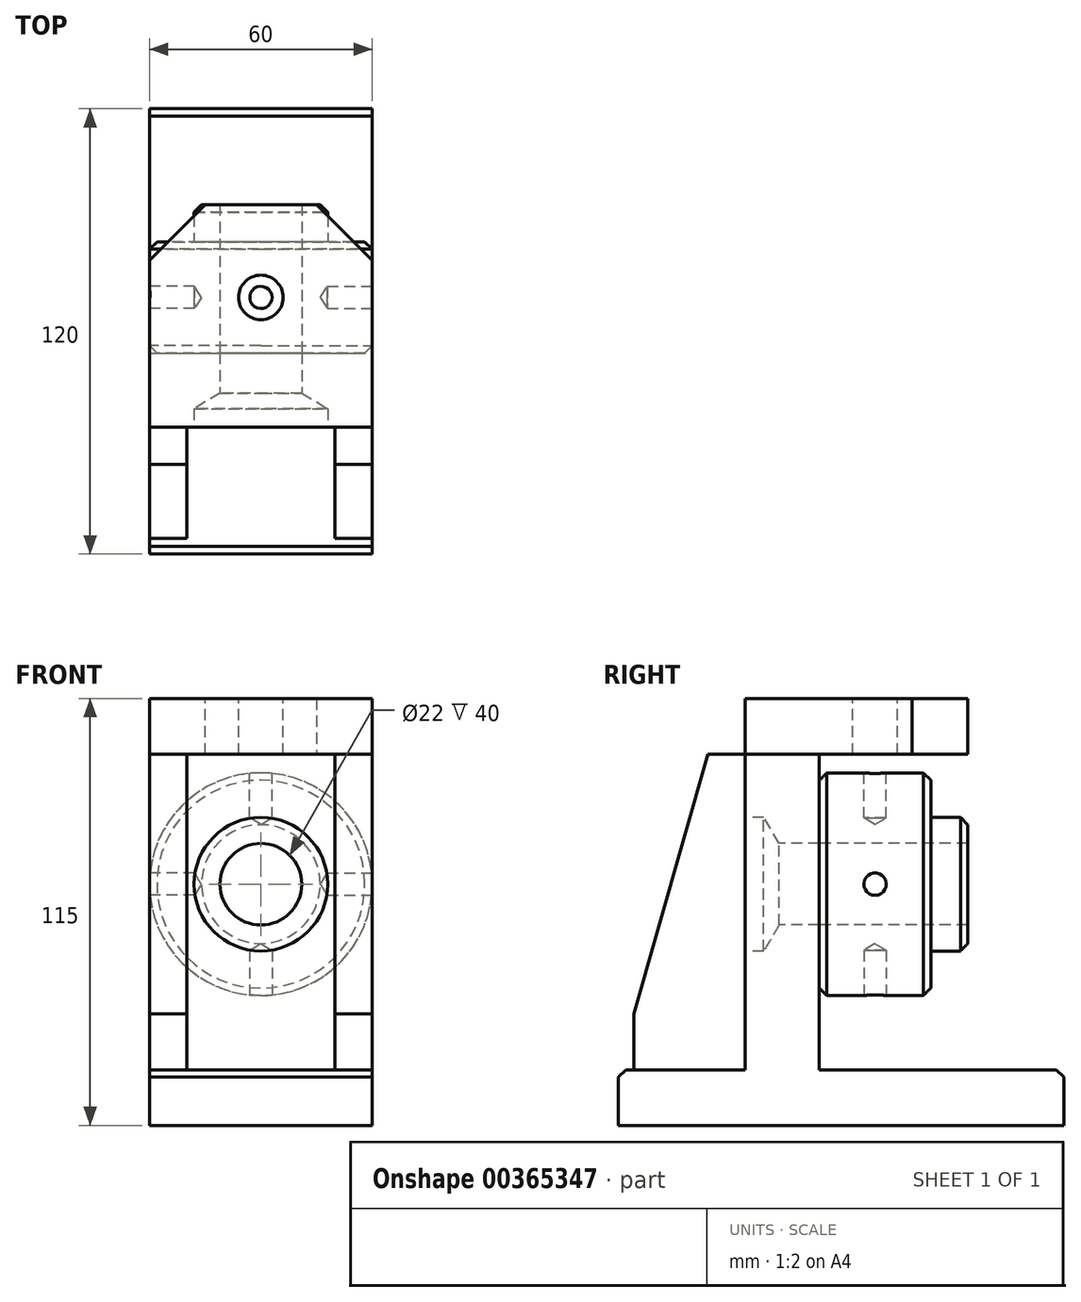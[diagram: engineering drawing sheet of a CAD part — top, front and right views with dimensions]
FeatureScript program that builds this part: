
annotation { "Feature Type Name" : "Feature", "Feature Type Description" : "" }
export const myFeature = defineFeature(function(context is Context, id is Id, definition is map)
    precondition{}
    {
        {
            var Q0;
            Q0=qCreatedBy(makeId("Right.planeOp"),FACE);
            var sketch = newSketch(context, id + "F0", { "sketchPlane" : qUnion([Q0])});
            skLineSegment(sketch, "E0", {"start": v(0, 11) * mm, "end": v(40, 11) * mm});
            skLineSegment(sketch, "E1", {"start": v(40, 11) * mm, "end": v(40, 18) * mm});
            skLineSegment(sketch, "E2", {"start": v(40, 18) * mm, "end": v(30, 18) * mm});
            skLineSegment(sketch, "E3", {"start": v(30, 18) * mm, "end": v(30, 30) * mm});
            skLineSegment(sketch, "E4", {"start": v(30, 30) * mm, "end": v(0, 30) * mm});
            skLineSegment(sketch, "E5", {"start": v(0, 30) * mm, "end": v(0, 11) * mm});
            skLineSegment(sketch, "E6", {"start": v(-74.8, 0) * mm, "end": v(75.55, 0) * mm, "construction": true});
            skSolve(sketch);
        }
        {
            var Q0;
            Q0 = qSketchRegion(id + "F0", true);
            var Q1;
            Q1=sQuery(id+"F0.wireOp",EDGE,"E6");
            revolve(context, id + "F1", {"entities" : qUnion([Q0]), "axis" : qUnion([Q1]), "revolveType" : RevolveType.FULL});
        }
        {
            var Q0;
            Q0=makeQuery(id+"F1.opRevolve","SWEPT_EDGE",EDGE,{"disambiguationData":[OSD([sQuery(id+"F0.wireOp",EDGE,"E3"),sQuery(id+"F0.wireOp",EDGE,"E4")])]});
            var Q1;
            Q1=makeQuery(id+"F1.opRevolve","SWEPT_EDGE",EDGE,{"disambiguationData":[OSD([sQuery(id+"F0.wireOp",EDGE,"E4"),sQuery(id+"F0.wireOp",EDGE,"E5")])]});
            var Q2;
            Q2=makeQuery(id+"F1.opRevolve","SWEPT_EDGE",EDGE,{"disambiguationData":[OSD([sQuery(id+"F0.wireOp",EDGE,"E1"),sQuery(id+"F0.wireOp",EDGE,"E2")])]});
            chamfer(context, id + "F2", {"entities" : qUnion([Q0, Q1, Q2]), "width" : 2 * mm, "tangentPropagation" : true});
        }
        {
            var Q0;
            Q0=qCreatedBy(makeId("Right.planeOp"),FACE);
            cPlane(context, id + "F3", {"entities" : qUnion([Q0]), "cplaneType" : CPlaneType.OFFSET, "offset" : 30 * mm, "width" : 150 * mm, "height" : 150 * mm});
        }
        {
            var Q0;
            Q0=qCreatedBy(id+"F3.planeOp",FACE);
            var sketch = newSketch(context, id + "F4", { "sketchPlane" : qUnion([Q0])});
            skCircle(sketch, "E7", {"center": v(15, 0) * mm, "radius": 3 * mm});
            skSolve(sketch);
        }
        {
            var Q0;
            Q0=sQuery(id+"F4.wireOp",VERTEX,"E7.center");
            var Q1;
            Q1=makeQuery(id+"F1.opRevolve","SWEPT_BODY",BODY,{"disambiguationData":[OSD([sQuery(id+"F0.wireOp",EDGE,"E0"),sQuery(id+"F0.wireOp",EDGE,"E1"),sQuery(id+"F0.wireOp",EDGE,"E2"),sQuery(id+"F0.wireOp",EDGE,"E3"),sQuery(id+"F0.wireOp",EDGE,"E4"),sQuery(id+"F0.wireOp",EDGE,"E5")])]});
            hole(context, id + "F5", {"style" : HoleStyle.SIMPLE, "endStyle" : HoleEndStyle.BLIND, "holeDiameter" : 6 * mm, "holeDepth" : 12 * mm, "isTappedThrough" : true, "tappedDepth" : 12 * mm, "tapClearance" : 3, "locations" : qUnion([Q0]), "scope" : qUnion([Q1])});
        }
        {
            var Q0;
            Q0=qCreatedBy(makeId("Top.planeOp"),FACE);
            cPlane(context, id + "F6", {"entities" : qUnion([Q0]), "cplaneType" : CPlaneType.OFFSET, "offset" : 30 * mm, "width" : 150 * mm, "height" : 150 * mm});
        }
        {
            var Q0;
            Q0=qCreatedBy(id+"F6.planeOp",FACE);
            var sketch = newSketch(context, id + "F7", { "sketchPlane" : qUnion([Q0])});
            skCircle(sketch, "E8", {"center": v(0, 15) * mm, "radius": 3 * mm});
            skSolve(sketch);
        }
        {
            var Q0;
            Q0=sQuery(id+"F7.wireOp",VERTEX,"E8.center");
            var Q1;
            Q1=makeQuery(id+"F1.opRevolve","SWEPT_BODY",BODY,{"disambiguationData":[OSD([sQuery(id+"F0.wireOp",EDGE,"E0"),sQuery(id+"F0.wireOp",EDGE,"E1"),sQuery(id+"F0.wireOp",EDGE,"E2"),sQuery(id+"F0.wireOp",EDGE,"E3"),sQuery(id+"F0.wireOp",EDGE,"E4"),sQuery(id+"F0.wireOp",EDGE,"E5")])]});
            hole(context, id + "F8", {"style" : HoleStyle.SIMPLE, "endStyle" : HoleEndStyle.BLIND, "holeDiameter" : 6 * mm, "holeDepth" : 12 * mm, "isTappedThrough" : true, "tappedDepth" : 12 * mm, "tapClearance" : 3, "locations" : qUnion([Q0]), "scope" : qUnion([Q1])});
        }
        {
            var Q0;
            Q0=qCreatedBy(makeId("Top.planeOp"),FACE);
            cPlane(context, id + "F9", {"entities" : qUnion([Q0]), "cplaneType" : CPlaneType.OFFSET, "offset" : 30 * mm, "oppositeDirection" : true, "width" : 150 * mm, "height" : 150 * mm});
        }
        {
            var Q0;
            Q0=qCreatedBy(id+"F9.planeOp",FACE);
            var sketch = newSketch(context, id + "F10", { "sketchPlane" : qUnion([Q0])});
            skCircle(sketch, "E9", {"center": v(0, 15) * mm, "radius": 3 * mm});
            skSolve(sketch);
        }
        {
            var Q0;
            Q0=sQuery(id+"F10.wireOp",VERTEX,"E9.center");
            var Q1;
            Q1=makeQuery(id+"F1.opRevolve","SWEPT_BODY",BODY,{"disambiguationData":[OSD([sQuery(id+"F0.wireOp",EDGE,"E0"),sQuery(id+"F0.wireOp",EDGE,"E1"),sQuery(id+"F0.wireOp",EDGE,"E2"),sQuery(id+"F0.wireOp",EDGE,"E3"),sQuery(id+"F0.wireOp",EDGE,"E4"),sQuery(id+"F0.wireOp",EDGE,"E5")])]});
            hole(context, id + "F11", {"style" : HoleStyle.SIMPLE, "endStyle" : HoleEndStyle.BLIND, "oppositeDirection" : true, "holeDiameter" : 6 * mm, "holeDepth" : 12 * mm, "isTappedThrough" : true, "tappedDepth" : 12 * mm, "tapClearance" : 3, "locations" : qUnion([Q0]), "scope" : qUnion([Q1])});
        }
        {
            var Q0;
            Q0=qCreatedBy(makeId("Right.planeOp"),FACE);
            cPlane(context, id + "F12", {"entities" : qUnion([Q0]), "cplaneType" : CPlaneType.OFFSET, "offset" : 30 * mm, "oppositeDirection" : true, "width" : 150 * mm, "height" : 150 * mm});
        }
        {
            var Q0;
            Q0=qCreatedBy(id+"F12.planeOp",FACE);
            var sketch = newSketch(context, id + "F13", { "sketchPlane" : qUnion([Q0])});
            skCircle(sketch, "E10", {"center": v(15, 0) * mm, "radius": 3 * mm});
            skSolve(sketch);
        }
        {
            var Q0;
            Q0=sQuery(id+"F13.wireOp",VERTEX,"E10.center");
            var Q1;
            Q1=makeQuery(id+"F1.opRevolve","SWEPT_BODY",BODY,{"disambiguationData":[OSD([sQuery(id+"F0.wireOp",EDGE,"E0"),sQuery(id+"F0.wireOp",EDGE,"E1"),sQuery(id+"F0.wireOp",EDGE,"E2"),sQuery(id+"F0.wireOp",EDGE,"E3"),sQuery(id+"F0.wireOp",EDGE,"E4"),sQuery(id+"F0.wireOp",EDGE,"E5")])]});
            hole(context, id + "F14", {"style" : HoleStyle.SIMPLE, "endStyle" : HoleEndStyle.BLIND, "oppositeDirection" : true, "holeDiameter" : 6 * mm, "holeDepth" : 12 * mm, "isTappedThrough" : true, "tappedDepth" : 12 * mm, "tapClearance" : 3, "locations" : qUnion([Q0]), "scope" : qUnion([Q1])});
        }
        {
            var Q0;
            Q0=qCreatedBy(makeId("Top.planeOp"),FACE);
            cPlane(context, id + "F15", {"entities" : qUnion([Q0]), "cplaneType" : CPlaneType.OFFSET, "offset" : 35 * mm, "width" : 150 * mm, "height" : 150 * mm});
        }
        {
            var Q0;
            Q0=qCreatedBy(id+"F15.planeOp",FACE);
            var sketch = newSketch(context, id + "F16", { "sketchPlane" : qUnion([Q0])});
            skLineSegment(sketch, "E11.left", {"start": v(30, 0) * mm, "end": v(30, 30) * mm});
            skLineSegment(sketch, "E11.right", {"start": v(-30, 0) * mm, "end": v(-30, 30) * mm});
            skPoint(sketch, "E11.middle", {"position": v(0, 0) * mm});
            skLineSegment(sketch, "E12", {"start": v(-30, 30) * mm, "end": v(-30, 40) * mm});
            skLineSegment(sketch, "E13", {"start": v(-30, 40) * mm, "end": v(30, 40) * mm});
            skLineSegment(sketch, "E14", {"start": v(30, 40) * mm, "end": v(30, 30) * mm});
            skLineSegment(sketch, "E15", {"start": v(-30, 0) * mm, "end": v(-30, -20) * mm});
            skLineSegment(sketch, "E16", {"start": v(-30, -20) * mm, "end": v(30, -20) * mm});
            skLineSegment(sketch, "E17", {"start": v(30, -20) * mm, "end": v(30, 0) * mm});
            skSolve(sketch);
        }
        {
            var Q0;
            Q0 = qSketchRegion(id + "F16", true);
            extrude(context, id + "F17", {"entities" : qUnion([Q0]), "depth" : 15 * mm});
        }
        {
            var Q0;
            Q0=makeQuery(id+"F17.opExtrude","SWEPT_EDGE",EDGE,{"disambiguationData":[OSD([sQuery(id+"F16.wireOp",EDGE,"E13"),sQuery(id+"F16.wireOp",EDGE,"E14")])]});
            var Q1;
            Q1=makeQuery(id+"F17.opExtrude","SWEPT_EDGE",EDGE,{"disambiguationData":[OSD([sQuery(id+"F16.wireOp",EDGE,"E12"),sQuery(id+"F16.wireOp",EDGE,"E13")])]});
            chamfer(context, id + "F18", {"entities" : qUnion([Q0, Q1]), "width" : 15 * mm, "tangentPropagation" : true});
        }
        {
            var Q0;
            Q0=makeQuery(id+"F17.opExtrude","CAP_FACE",FACE,{"disambiguationData":[OSD([sQuery(id+"F16.wireOp",EDGE,"E11.left"),sQuery(id+"F16.wireOp",EDGE,"E11.right"),sQuery(id+"F16.wireOp",EDGE,"E12"),sQuery(id+"F16.wireOp",EDGE,"E13"),sQuery(id+"F16.wireOp",EDGE,"E14"),sQuery(id+"F16.wireOp",EDGE,"E15"),sQuery(id+"F16.wireOp",EDGE,"E16"),sQuery(id+"F16.wireOp",EDGE,"E17")])],"isStart":false});
            var sketch = newSketch(context, id + "F19", { "sketchPlane" : qUnion([Q0])});
            skCircle(sketch, "E18", {"center": v(0, 15) * mm, "radius": 6 * mm});
            skSolve(sketch);
        }
        {
            var Q0;
            Q0=sQuery(id+"F19.wireOp",VERTEX,"E18.center");
            var Q1;
            Q1=makeQuery(id+"F17.opExtrude","SWEPT_BODY",BODY,{"disambiguationData":[OSD([sQuery(id+"F16.wireOp",EDGE,"E11.left"),sQuery(id+"F16.wireOp",EDGE,"E11.right"),sQuery(id+"F16.wireOp",EDGE,"E12"),sQuery(id+"F16.wireOp",EDGE,"E13"),sQuery(id+"F16.wireOp",EDGE,"E14"),sQuery(id+"F16.wireOp",EDGE,"E15"),sQuery(id+"F16.wireOp",EDGE,"E16"),sQuery(id+"F16.wireOp",EDGE,"E17")])]});
            hole(context, id + "F20", {"style" : HoleStyle.SIMPLE, "endStyle" : HoleEndStyle.BLIND, "holeDiameter" : 12 * mm, "holeDepth" : 15 * mm, "isTappedThrough" : true, "tappedDepth" : 12 * mm, "tapClearance" : 3, "locations" : qUnion([Q0]), "scope" : qUnion([Q1])});
        }
        {
            var Q0;
            Q0=qCreatedBy(makeId("Front.planeOp"),FACE);
            cPlane(context, id + "F21", {"entities" : qUnion([Q0]), "cplaneType" : CPlaneType.OFFSET, "offset" : 20 * mm, "width" : 150 * mm, "height" : 150 * mm});
        }
        {
            var Q0;
            Q0=qCreatedBy(id+"F21.planeOp",FACE);
            var sketch = newSketch(context, id + "F22", { "sketchPlane" : qUnion([Q0])});
            skLineSegment(sketch, "E19.bottom", {"start": v(30, -50) * mm, "end": v(-30, -50) * mm});
            skLineSegment(sketch, "E19.left", {"start": v(30, -50) * mm, "end": v(30, 35) * mm});
            skLineSegment(sketch, "E19.right", {"start": v(-30, -50) * mm, "end": v(-30, 35) * mm});
            skPoint(sketch, "E19.middle", {"position": v(0, 0) * mm});
            skLineSegment(sketch, "E20", {"start": v(-30, 35) * mm, "end": v(30, 35) * mm});
            skSolve(sketch);
        }
        {
            var Q0;
            Q0 = qSketchRegion(id + "F22", true);
            extrude(context, id + "F23", {"entities" : qUnion([Q0]), "oppositeDirection" : true, "depth" : 20 * mm});
        }
        {
            var Q0;
            Q0=qCreatedBy(id+"F3.planeOp",FACE);
            var sketch = newSketch(context, id + "F24", { "sketchPlane" : qUnion([Q0])});
            skLineSegment(sketch, "E21", {"start": v(0, 0) * mm, "end": v(0, -50) * mm});
            skLineSegment(sketch, "E22", {"start": v(-20, -50) * mm, "end": v(-20, 0) * mm});
            skLineSegment(sketch, "E23.bottom", {"start": v(-54.13, -50) * mm, "end": v(65.87, -50) * mm});
            skLineSegment(sketch, "E23.top", {"start": v(-54.13, -65) * mm, "end": v(65.87, -65) * mm});
            skLineSegment(sketch, "E23.left", {"start": v(-54.13, -50) * mm, "end": v(-54.13, -65) * mm});
            skLineSegment(sketch, "E23.right", {"start": v(65.87, -50) * mm, "end": v(65.87, -65) * mm});
            skSolve(sketch);
        }
        {
            var Q0;
            Q0 = qSketchRegion(id + "F24", true);
            extrude(context, id + "F25", {"entities" : qUnion([Q0]), "operationType" : NewBodyOperationType.ADD, "oppositeDirection" : true, "depth" : 60 * mm});
        }
        {
            var Q0;
            Q0=qCreatedBy(id+"F21.planeOp",FACE);
            var sketch = newSketch(context, id + "F26", { "sketchPlane" : qUnion([Q0])});
            skCircle(sketch, "E24", {"center": v(0, 0) * mm, "radius": 18 * mm});
            skSolve(sketch);
        }
        {
            var Q0;
            Q0=sQuery(id+"F26.wireOp",VERTEX,"E24.center");
            var Q1;
            Q1=makeQuery(id+"F23.opExtrude","SWEPT_BODY",BODY,{"disambiguationData":[OSD([sQuery(id+"F22.wireOp",EDGE,"E19.bottom"),sQuery(id+"F22.wireOp",EDGE,"E19.left"),sQuery(id+"F22.wireOp",EDGE,"E19.right"),sQuery(id+"F22.wireOp",EDGE,"E20")])]});
            hole(context, id + "F27", {"style" : HoleStyle.SIMPLE, "endStyle" : HoleEndStyle.BLIND, "holeDiameter" : 36 * mm, "holeDepth" : 5 * mm, "isTappedThrough" : true, "tappedDepth" : 12 * mm, "tapClearance" : 3, "startFromSketch" : true, "locations" : qUnion([Q0]), "scope" : qUnion([Q1])});
        }
        {
            var Q0;
            Q0=qCreatedBy(id+"F21.planeOp",FACE);
            var sketch = newSketch(context, id + "F28", { "sketchPlane" : qUnion([Q0])});
            skCircle(sketch, "E25", {"center": v(0, 0) * mm, "radius": 11 * mm});
            skSolve(sketch);
        }
        {
            var Q0;
            Q0=sQuery(id+"F28.wireOp",VERTEX,"E25.center");
            var Q1;
            Q1=makeQuery(id+"F23.opExtrude","SWEPT_BODY",BODY,{"disambiguationData":[OSD([sQuery(id+"F22.wireOp",EDGE,"E19.bottom"),sQuery(id+"F22.wireOp",EDGE,"E19.left"),sQuery(id+"F22.wireOp",EDGE,"E19.right"),sQuery(id+"F22.wireOp",EDGE,"E20")])]});
            hole(context, id + "F29", {"style" : HoleStyle.SIMPLE, "endStyle" : HoleEndStyle.BLIND, "holeDiameter" : 22 * mm, "holeDepth" : 100 * mm, "isTappedThrough" : true, "tappedDepth" : 12 * mm, "tapClearance" : 3, "startFromSketch" : true, "locations" : qUnion([Q0]), "scope" : qUnion([Q1])});
        }
        {
            var Q0;
            Q0=makeQuery(id+"F25.opExtrude","SWEPT_EDGE",EDGE,{"disambiguationData":[OSD([sQuery(id+"F24.wireOp",EDGE,"E23.bottom"),sQuery(id+"F24.wireOp",EDGE,"E23.left")])]});
            var Q1;
            Q1=makeQuery(id+"F25.opExtrude","SWEPT_EDGE",EDGE,{"disambiguationData":[OSD([sQuery(id+"F24.wireOp",EDGE,"E23.bottom"),sQuery(id+"F24.wireOp",EDGE,"E23.right")])]});
            chamfer(context, id + "F30", {"entities" : qUnion([Q0, Q1]), "width" : 2 * mm, "tangentPropagation" : true});
        }
        {
            var Q0;
            Q0=qCreatedBy(id+"F3.planeOp",FACE);
            var sketch = newSketch(context, id + "F31", { "sketchPlane" : qUnion([Q0])});
            skLineSegment(sketch, "E26", {"start": v(0, 0) * mm, "end": v(-20, 0) * mm});
            skLineSegment(sketch, "E27", {"start": v(-20, 0) * mm, "end": v(-20, 35) * mm});
            skLineSegment(sketch, "E28", {"start": v(-20, 0) * mm, "end": v(-20, -50) * mm});
            skLineSegment(sketch, "E29", {"start": v(-20, -50) * mm, "end": v(-50, -50) * mm});
            skLineSegment(sketch, "E30", {"start": v(-50, -50) * mm, "end": v(-50, -35) * mm});
            skLineSegment(sketch, "E31", {"start": v(-20, 35) * mm, "end": v(-30, 35) * mm});
            skLineSegment(sketch, "E32", {"start": v(-30, 35) * mm, "end": v(-50, -35) * mm});
            skSolve(sketch);
        }
        {
            var Q0;
            Q0=makeQuery(id+"F31.imprint","IMPRINT",FACE,{"disambiguationData":[TD([[makeQuery(id+"F31.imprint","IMPRINT",EDGE,{"derivedFrom":sQuery(id+"F31.wireOp",EDGE,"E27")}),1.0]])]});
            extrude(context, id + "F32", {"entities" : qUnion([Q0]), "oppositeDirection" : true, "depth" : 10 * mm});
        }
        {
            var Q0;
            Q0=qCreatedBy(id+"F12.planeOp",FACE);
            var sketch = newSketch(context, id + "F33", { "sketchPlane" : qUnion([Q0])});
            skLineSegment(sketch, "E33", {"start": v(0, 0) * mm, "end": v(-20, 0) * mm});
            skLineSegment(sketch, "E34", {"start": v(-20, 0) * mm, "end": v(-20, 35.02) * mm});
            skLineSegment(sketch, "E35", {"start": v(-20, 0) * mm, "end": v(-20, 35) * mm});
            skLineSegment(sketch, "E36", {"start": v(-20, 0) * mm, "end": v(-20, -50) * mm});
            skLineSegment(sketch, "E37", {"start": v(-20, -50) * mm, "end": v(-50, -50) * mm});
            skLineSegment(sketch, "E38", {"start": v(-50, -50) * mm, "end": v(-50, -35) * mm});
            skLineSegment(sketch, "E39", {"start": v(-20, 35.02) * mm, "end": v(-30, 35.02) * mm});
            skLineSegment(sketch, "E40", {"start": v(-30, 35.02) * mm, "end": v(-50, -35) * mm});
            skSolve(sketch);
        }
        {
            var Q0;
            Q0=makeQuery(id+"F33.imprint","IMPRINT",FACE,{"disambiguationData":[TD([[makeQuery(id+"F33.imprint","IMPRINT",EDGE,{"derivedFrom":sQuery(id+"F33.wireOp",EDGE,"E34")}),1.0]])]});
            extrude(context, id + "F34", {"entities" : qUnion([Q0]), "depth" : 10 * mm});
        }
    });
